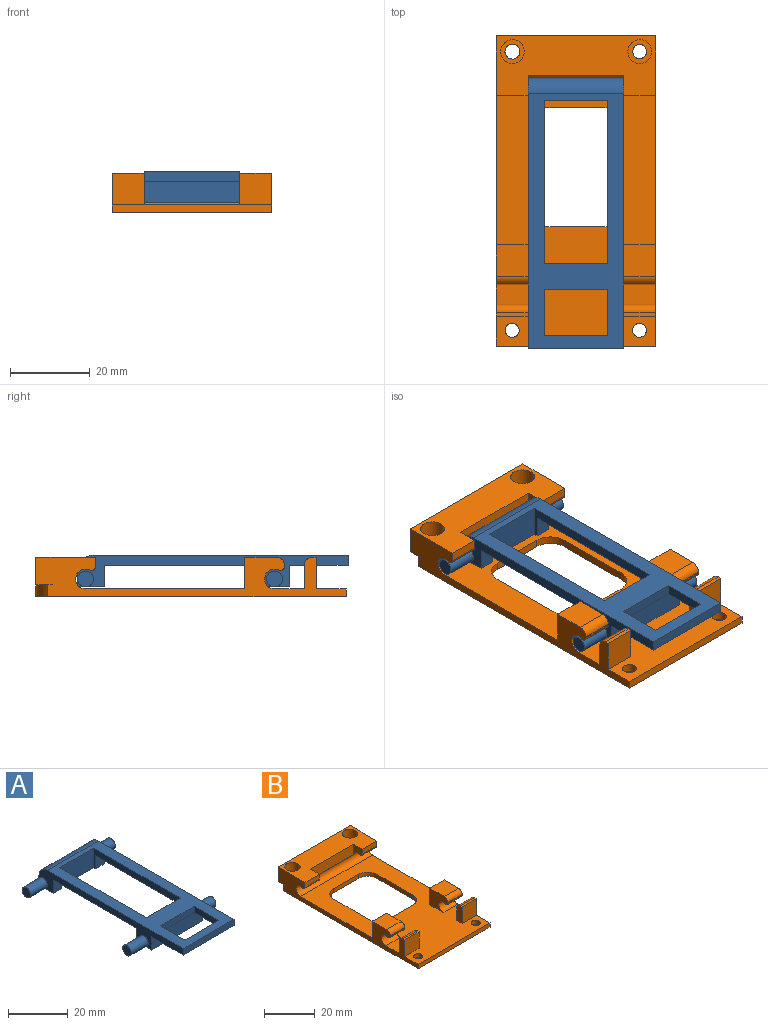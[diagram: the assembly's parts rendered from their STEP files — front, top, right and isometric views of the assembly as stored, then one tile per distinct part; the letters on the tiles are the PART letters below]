
ASSEMBLY  parts=2 mates=1
PART A: 34 faces, bbox 40x68x8 mm
  f0: plane 5.43x4mm, normal (0,-1,0), area 21.7mm2, adj f1,f5,f6,f33
  f1: plane 39.31x4mm, normal (0,0,-1), area 157.3mm2, adj f0,f2,f6,f33
  f2: plane 5.43x4mm, normal (0,1,0), area 21.7mm2, adj f1,f4,f6,f33
  f3: plane 24x2.57mm, normal (0,-1,0), area 61.7mm2, adj f6,f7,f11,f24
  f4: plane 24x7.1mm, normal (0,0,-1), area 160.7mm2, adj f2,f6,f7,f22,f23,f30,f32,f33
  f5: plane 24x6.75mm, normal (0,0,-1), area 146.3mm2, adj f0,f6,f7,f8,f9,f10,f20,f31
  f6: plane 68x8mm, normal (1,0,0), area 220.7mm2, adj f0,f1,f2,f3,f4,f5,f10,f11
  f7: plane 68x8mm, normal (-1,0,0), area 220.7mm2, adj f3,f4,f5,f10,f11,f13,f17,f20
  f8: plane 2x2mm, normal (1,0,0), area 0.9mm2, adj f5,f10,f14
  f9: plane 2x2mm, normal (-1,0,0), area 0.9mm2, adj f5,f10,f13
  f10: plane 24x4mm, normal (0,1,0), area 96mm2, adj f5,f6,f7,f8,f9,f25
  f11: plane 64x24mm, normal (0,0,1), area 696.3mm2, adj f3,f6,f7,f25,f26,f27,f28,f29
  f12: plane 4x4mm, normal (-1,0,0), area 12.6mm2, adj f13
  f13: cylinder r=2mm len=8mm, axis (-1,0,0), area 100.5mm2, adj f7,f9,f12
  f14: cylinder r=2mm len=8mm, axis (-1,0,0), area 100.5mm2, adj f6,f8,f15
  f15: plane 4x4mm, normal (1,0,0), area 12.6mm2, adj f14
  f16: plane 4x4mm, normal (-1,0,0), area 12.6mm2, adj f17
  f17: cylinder r=2mm len=8mm, axis (-1,0,0), area 100.5mm2, adj f7,f16
  f18: cylinder r=2mm len=8mm, axis (-1,0,0), area 100.5mm2, adj f6,f19
  f19: plane 4x4mm, normal (1,0,0), area 12.6mm2, adj f18
  f20: plane 5.43x4mm, normal (0,-1,0), area 21.7mm2, adj f5,f7,f21,f32
  f21: plane 39.31x4mm, normal (0,0,-1), area 157.3mm2, adj f7,f20,f22,f32
  f22: plane 5.43x4mm, normal (0,1,0), area 21.7mm2, adj f4,f7,f21,f32
  f23: plane 24x5.43mm, normal (0,-1,0), area 130.3mm2, adj f4,f6,f7,f24
  f24: plane 24x14.83mm, normal (0,0,-1), area 170.8mm2, adj f3,f6,f7,f23,f26,f27,f28,f29
  f25: cylinder r=4mm len=24mm, axis (1,0,0), area 150.8mm2, adj f6,f7,f10,f11
  f26: plane 11.56x2.57mm, normal (1,0,0), area 29.7mm2, adj f11,f24,f27,f29
  f27: plane 16x2.57mm, normal (0,1,0), area 41.1mm2, adj f11,f24,f26,f28
  f28: plane 11.56x2.57mm, normal (-1,0,0), area 29.7mm2, adj f11,f24,f27,f29
  f29: plane 16x2.57mm, normal (0,-1,0), area 41.1mm2, adj f11,f24,f26,f28
  f30: plane 16x8mm, normal (0,1,0), area 128mm2, adj f4,f11,f32,f33
  f31: plane 16x8mm, normal (0,-1,0), area 128mm2, adj f5,f11,f32,f33
  f32: plane 40.92x8mm, normal (1,0,0), area 113.9mm2, adj f4,f5,f11,f20,f21,f22,f30,f31
  f33: plane 40.92x8mm, normal (-1,0,0), area 113.9mm2, adj f0,f1,f2,f4,f5,f11,f30,f31
PART B: 65 faces, bbox 40.1x78x10 mm
  f0: plane 8x2.34mm, normal (0,-1,0), area 18.7mm2, adj f1,f7,f32,f63
  f1: plane 40.08x15mm, normal (0,0,1), area 424.1mm2, adj f0,f6,f7,f20,f23,f49,f51,f61
  f2: cylinder r=2.5mm len=40.01mm, axis (-1,0,0), area 249.8mm2, adj f3,f6,f7,f21,f32,f62,f63,f64
  f3: cylinder r=1mm len=8mm, axis (-1,0,0), area 16.1mm2, adj f2,f6,f20,f62
  f4: cylinder r=1.88mm len=3.76mm, axis (0,0,-1), area 23.6mm2, adj f46,f52
  f5: cylinder r=1.77mm len=3.54mm, axis (0,0,-1), area 22.2mm2, adj f45,f50
  f6: plane 78x10mm, normal (-1,0,0), area 325.5mm2, adj f1,f2,f3,f8,f16,f18,f19,f20
  f7: plane 15.03x10.03mm, normal (1,-0.01,0), area 116.8mm2, adj f0,f1,f2,f8,f11,f21,f23,f32
  f8: plane 78x40.06mm, normal (0,0,-1), area 2237.1mm2, adj f6,f7,f11,f22,f23,f24,f25,f41
  f9: plane 10x8mm, normal (-1,0,0), area 57.2mm2, adj f15,f21,f27,f28,f35,f36,f40
  f10: plane 10x8mm, normal (1,0,0), area 57.2mm2, adj f16,f21,f29,f30,f33,f34,f39
  f11: plane 63x10mm, normal (1,0,0), area 206.3mm2, adj f7,f8,f12,f14,f15,f21,f22,f26
  f12: plane 8x6mm, normal (0,1,0), area 48mm2, adj f11,f13,f21,f38
  f13: plane 8x3mm, normal (-1,0,0), area 23.1mm2, adj f12,f14,f21,f26,f38
  f14: plane 8x1mm, normal (0,0,1), area 8mm2, adj f11,f13,f26,f38
  f15: plane 8x0.34mm, normal (0,-1,0), area 2.7mm2, adj f9,f11,f36,f40
  f16: plane 8x0.34mm, normal (0,-1,0), area 2.7mm2, adj f6,f10,f33,f39
  f17: plane 8x3mm, normal (1,0,0), area 23.1mm2, adj f18,f19,f21,f31,f37
  f18: plane 8x6mm, normal (0,1,0), area 48mm2, adj f6,f17,f21,f37
  f19: plane 8x1mm, normal (0,0,1), area 8mm2, adj f6,f17,f31,f37
  f20: plane 8x2.34mm, normal (0,-1,0), area 18.7mm2, adj f1,f3,f6,f62
  f21: plane 65.5x40.01mm, normal (0,0,1), area 1734.2mm2, adj f2,f6,f7,f9,f10,f11,f12,f13
  f22: plane 40x2mm, normal (0,-1,0), area 80mm2, adj f6,f8,f11,f21
  f23: plane 40.08x10mm, normal (0,1,0), area 288.1mm2, adj f1,f6,f7,f8,f41,f45,f46,f47
  f24: cylinder r=1.75mm len=3.5mm, axis (0,0,-1), area 22mm2, adj f8,f21
  f25: cylinder r=1.75mm len=3.5mm, axis (0,0,-1), area 22mm2, adj f8,f21
  f26: plane 8x8mm, normal (0,-1,0), area 64mm2, adj f11,f13,f14,f21
  f27: plane 8x8mm, normal (0,1,0), area 64mm2, adj f9,f11,f21,f28
  f28: plane 8x8mm, normal (0,0,1), area 64mm2, adj f9,f11,f27,f40
  f29: plane 8x8mm, normal (0,1,0), area 64mm2, adj f6,f10,f21,f30
  f30: plane 8x8mm, normal (0,0,1), area 64mm2, adj f6,f10,f29,f39
  f31: plane 8x8mm, normal (0,-1,0), area 64mm2, adj f6,f17,f19,f21
  f32: cylinder r=1mm len=8.01mm, axis (-1,0,0), area 16.1mm2, adj f0,f2,f7,f63
  f33: cylinder r=1mm len=8mm, axis (-1,0,0), area 16.1mm2, adj f6,f10,f16,f34
  f34: cylinder r=2.5mm len=8mm, axis (-1,0,0), area 71.7mm2, adj f6,f10,f21,f33
  f35: cylinder r=2.5mm len=8mm, axis (-1,0,0), area 71.7mm2, adj f9,f11,f21,f36
  f36: cylinder r=1mm len=8mm, axis (-1,0,0), area 16.1mm2, adj f9,f11,f15,f35
  f37: cylinder r=2mm len=8mm, axis (-1,0,0), area 25.1mm2, adj f6,f17,f18,f19
  f38: cylinder r=2mm len=8mm, axis (-1,0,0), area 25.1mm2, adj f11,f12,f13,f14
  f39: cylinder r=2mm len=8mm, axis (-1,0,0), area 25.1mm2, adj f6,f10,f16,f30
  f40: cylinder r=2mm len=8mm, axis (-1,0,0), area 25.1mm2, adj f9,f11,f15,f28
  f41: cylinder r=13.19mm len=9.26mm, axis (0,0,-1), area 32.7mm2, adj f8,f23,f42,f45
  f42: cylinder r=5mm len=4.49mm, axis (0,0,-1), area 16.7mm2, adj f8,f41,f43,f45
  f43: plane 3x0.06mm, normal (0,1,0), area 0.2mm2, adj f8,f42,f44,f45
  f44: cylinder r=5mm len=4.94mm, axis (0,0,-1), area 21.2mm2, adj f7,f8,f43,f45
  f45: plane 18.76x7.95mm, normal (0,0,-1), area 73mm2, adj f5,f7,f23,f41,f42,f43,f44
  f46: plane 18.82x7.96mm, normal (0,0,-1), area 71.8mm2, adj f4,f6,f23,f47,f48
  f47: cylinder r=13.19mm len=9.63mm, axis (0,0,-1), area 34.6mm2, adj f8,f23,f46,f48
  f48: cylinder r=5mm len=9.2mm, axis (0,0,-1), area 38.5mm2, adj f6,f8,f46,f47
  f49: cylinder r=3mm len=6mm, axis (0,0,1), area 94.2mm2, adj f1,f50
  f50: plane 6x6mm, normal (0,0,1), area 18.4mm2, adj f5,f49
  f51: cylinder r=3mm len=6mm, axis (0,0,1), area 94.2mm2, adj f1,f52
  f52: plane 6x6mm, normal (0,0,1), area 17.2mm2, adj f4,f51
  f53: cylinder r=5mm len=5mm, axis (0,0,1), area 15.7mm2, adj f8,f21,f54,f60
  f54: plane 14x2mm, normal (0,1,0), area 28mm2, adj f8,f21,f53,f55
  f55: cylinder r=5mm len=5mm, axis (0,0,1), area 15.7mm2, adj f8,f21,f54,f56
  f56: plane 20x2mm, normal (-1,0,0), area 40mm2, adj f8,f21,f55,f57
  f57: cylinder r=5mm len=5mm, axis (0,0,1), area 15.7mm2, adj f8,f21,f56,f58
  f58: plane 14x2mm, normal (0,-1,0), area 28mm2, adj f8,f21,f57,f59
  f59: cylinder r=5mm len=5mm, axis (0,0,1), area 15.7mm2, adj f8,f21,f58,f60
  f60: plane 20x2mm, normal (1,0,0), area 40mm2, adj f8,f21,f53,f59
  f61: plane 24x5mm, normal (0,-1,0), area 120mm2, adj f1,f62,f63,f64
  f62: plane 5x5mm, normal (1,0,0), area 16.7mm2, adj f1,f2,f3,f20,f61,f64
  f63: plane 5x5mm, normal (-1,0,0), area 16.7mm2, adj f0,f1,f2,f32,f61,f64
  f64: plane 24x0.05mm, normal (0,0,1), area 1.2mm2, adj f2,f61,f62,f63
PLACE A t=(-1.14,-4.69,-0.33)mm
PLACE B t=(-1.14,0.81,-2.83)mm
MATE cylindrical A.f13 <-> B.f2  axis (-1,0,0) through (-21.14,27.31,1.67)mm
